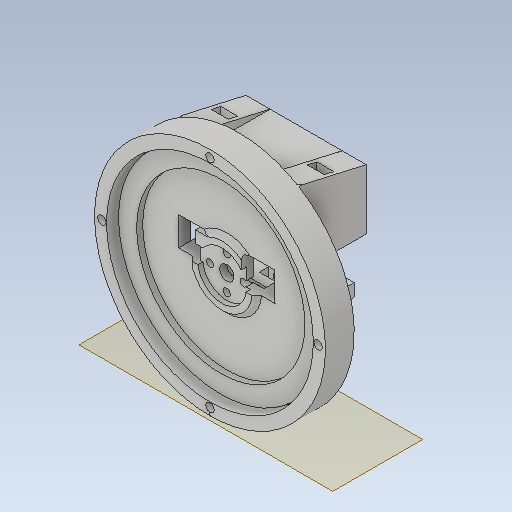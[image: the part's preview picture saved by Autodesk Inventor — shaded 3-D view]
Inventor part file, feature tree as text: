
AUTODESK INVENTOR PART (.ipt)
format: ipt  version: 2020.1 (Build 241239000, 239)  size: 489,984 bytes
history: native  units: mm
features: extrude x24, sketch x24, other x2, chamfer x1, plane x1
ambient origin geometry x8: Origin, YZ Plane, XZ Plane, XY Plane, X Axis, Y Axis, Z Axis, Center Point
bodies: Solid1 (feature_tree)
feature tree (52):
  extrude  "base"  Depth=5.0mm TaperAngle=0.0deg
  extrude  "wall"  Depth=86.0mm
  extrude  "servo_horn_place"  Depth=20.0mm
  chamfer  "Chamfer1"  Distance=2.0mm
  extrude  "attach_case"  Depth=45.0mm
  extrude  "servo_place"  Depth=40.0mm TaperAngle=360.0deg
  extrude  "servo_bed"  Depth=20.0mm
  extrude  "screw_holes"  Depth=40.0mm
  extrude  "screw_holes_prev"  Depth=40.0mm
  extrude  "gear_hole"  Depth=5.0mm
  extrude  "sliding_platform"  Depth=50.0mm
  extrude  "reinforcement_servo_place_1"  Depth=2.0mm TaperAngle=0.0deg
  extrude  "reinforcement_servo_place_2"  Depth=2.5mm
  extrude  "reinforcement_servo_place_3"  Depth=5.0mm
  extrude  "reinforcement_servo_place_4"  Depth=5.0mm
  extrude  "screw_hole_prev_cen"  Depth=3.5mm
  extrude  "servo_cable_hole"  Depth=10.0mm TaperAngle=0.0deg
  extrude  "Extrusion20"  Depth=3.0mm
  plane  "Work Plane1"
  extrude  "guide_arrow"  Depth=6.0mm TaperAngle=0.0deg
  other  "Edición directa1"
  extrude  "Extrusión23"  Depth=4.0mm TaperAngle=0.0deg
  extrude  "Extrusión24"  Depth=2.5mm TaperAngle=0.0deg
  extrude  "Extrusión25"  Depth=10.0mm TaperAngle=0.0deg
  extrude  "Extrusión26"  Depth=5.0mm
  extrude  "case_nut_holes_1"  Depth=10.0mm TaperAngle=0.0deg
  extrude  "case_nut_holes_2"  Depth=6.0mm
  sketch  "Sketch1"  dims[d0=96.0mm d1=5.0mm d2=0.0mm]
  sketch  "Sketch2"  dims[d3=96.0mm d4=86.0mm]
  sketch  "Sketch3"  dims[d5=7.0mm d6=0.0mm d7=20.0mm]
  sketch  "Sketch5"  dims[d8=25.0mm d9=2.0mm d10=0.0mm]
  sketch  "Sketch6"  dims[d12=2.0mm d13=2.0mm d14=45.0deg d18=45.0mm]
  sketch  "Sketch7"  dims[d19=3.5mm d20=40.0mm d22=360.0deg]
  sketch  "Sketch8"  dims[d24=2.0mm d25=0.0mm d26=20.0mm]
  sketch  "Sketch11"  dims[d27=10.0mm d28=40.0mm]
  sketch  "Sketch12"  dims[d29=40.0mm d30=40.0mm]
  sketch  "Sketch13"  dims[d31=5.0mm d32=5.0mm]
  sketch  "Sketch14"  dims[d33=50.0mm d34=50.0mm]
  sketch  "Sketch15"  dims[d35=22.0mm d36=0.0mm d37=2.0mm d38=0.0mm]
  sketch  "Sketch16"  dims[d39=20.0mm d40=2.5mm]
  sketch  "Sketch17"  dims[d41=3.5mm d42=5.0mm]
  sketch  "Sketch18"  dims[d43=2.5mm d44=5.0mm]
  sketch  "Sketch19"  dims[d45=2.5mm d46=3.5mm]
  sketch  "Sketch20"  dims[d47=3.5mm d48=10.0mm d49=0.0mm]
  sketch  "Sketch21"  dims[d65=7.0mm d66=3.0mm]
  sketch  "Boceto23"  dims[d67=40.0mm d69=360.0deg d71=6.0mm d72=0.0mm]
  sketch  "Boceto24"  dims[d74=25.0mm d75=4.0mm d76=0.0mm]
  sketch  "Boceto25"  dims[d77=70.0mm d78=2.5mm d79=0.0mm]
  sketch  "Boceto26"  dims[d83=15.0mm d84=10.0mm d85=0.0mm]
  sketch  "Sketch27"  dims[d86=10.0mm d87=0.0mm d88=5.0mm]
  sketch  "Sketch28"  dims[d89=10.0mm d90=0.0mm d91=10.0mm d92=0.0mm d93=6.0mm d94=10.0mm d95=0.0mm d96=9.0mm d97=10.0mm d98=10.0mm d99=1.0mm d100=10.0mm d101=0.0mm d102=3.0mm d103=10.0mm d104=0.0mm d105=4.0mm d106=45.0deg d107=1.5mm d108=5.0mm d109=4.0mm d110=135.0deg d113=1.5mm d114=1.0mm d115=0.0mm d125=0.0mm d126=0.0mm d127=30.0mm d128=10.0mm d129=0.0mm d130=8.0mm d131=0.0mm d132=6.6mm d133=1.8mm d134=90.0deg d135=6.6mm d137=2.0mm d138=0.0mm d139=3.0mm d140=0.0mm d141=12.0mm d142=3.5mm d143=4.0mm d144=7.0mm d145=12.0mm d146=3.5mm d147=4.0mm d148=90.0deg d149=7.0mm d150=15.0mm d151=0.0mm d152=12.0mm d153=90.0deg d154=3.5mm d155=180.0deg d156=4.0mm d157=7.0mm d158=15.0mm d159=0.0mm d160=9.0mm d161=180.0deg d162=10.0mm d163=10.0mm d164=10.0mm d165=1.0mm]
  other  "Desplazar1"
